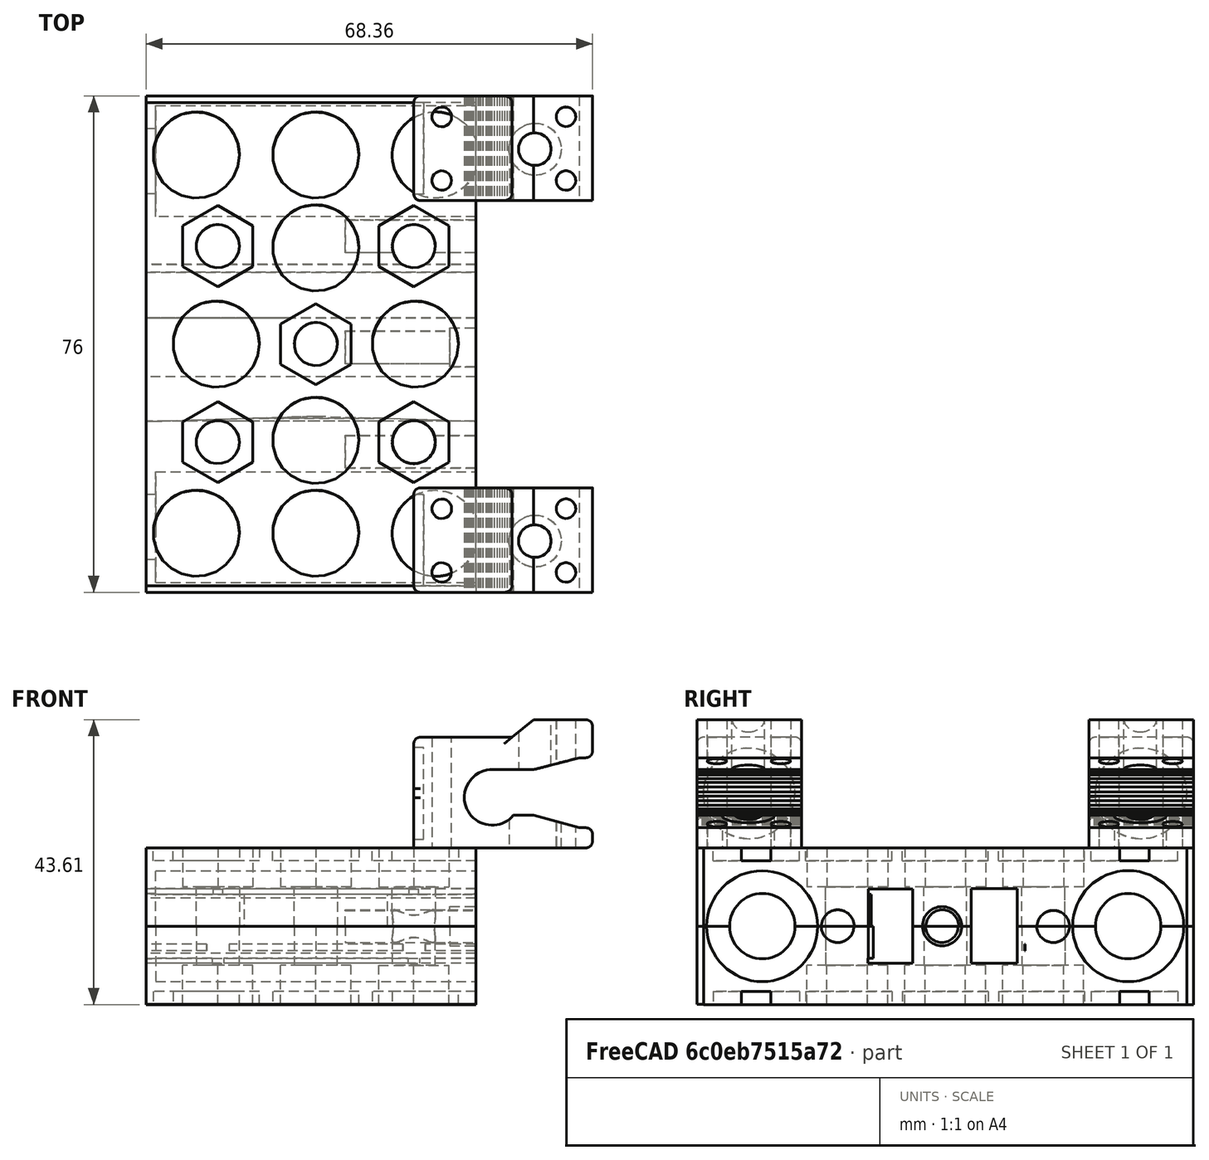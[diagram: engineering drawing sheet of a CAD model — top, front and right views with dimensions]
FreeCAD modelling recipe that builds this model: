
FCSTD DOCUMENT  (FreeCAD 0.21R33694 (Git))
Label: Universal_Axis_Z_Carriage
License: All rights reserved
LicenseURL: http://en.wikipedia.org/wiki/All_rights_reserved
objects: App::FeaturePython×12, Part::FeaturePython×3, Part::Compound×1
note: 4 computed .brp shape members not serialized (recipe doc carries the construction recipe); baked Part::Feature solids carry a one-line shape summary decoded from their .brp

FEATURE [Part::FeaturePython] b_Universal_Axis_Carriage_001_  label="Universal_Axis_Carriage_001"  # a2plus imported part (geometry in sourceFile) (typed FeaturePython)
  a2p_Version = 0.4.60n
  fixedPosition = true
  objectType = a2pPart
  sourceFile = ./Universal_Axis_Carriage.fcstd
  subassemblyImport = false
  timeLastImport = 1.70034e+09
  updateColors = true
FEATURE [Part::FeaturePython] b_Autoparallel_001_  label="Autoparallel_001"  # a2plus imported part (geometry in sourceFile) (typed FeaturePython)
  Placement = pos=(33.3346,-22,28.966) rot=(0,0.707107,-0.707107;3.14159rad)
  a2p_Version = 0.4.60n
  fixedPosition = false
  objectType = a2pPart
  sourceFile = ./Autoparallel.fcstd
  subassemblyImport = false
  timeLastImport = 1.68351e+09
  updateColors = true
FEATURE [App::FeaturePython] planeCoincident_001  label="planeCoincident_001__Universal_Axis_Carriage_001"  # a2plus constraint (typed FeaturePython)
  Object1 = b_Autoparallel_001_
  Object2 = b_Universal_Axis_Carriage_001_
  ParentTreeObject = -> b_Autoparallel_001_
  SubElement1 = Face15
  SubElement2 = Face156
  Suppressed = false
  Type = plane
  directionConstraint = 0
  offset = 0
FEATURE [App::FeaturePython] planeCoincident_001_mirror  label="planeCoincident_001__Autoparallel_001"  # a2plus constraint (typed FeaturePython)
  Object1 = b_Autoparallel_001_
  Object2 = b_Universal_Axis_Carriage_001_
  ParentTreeObject = -> b_Universal_Axis_Carriage_001_
  SubElement1 = Face15
  SubElement2 = Face156
  Suppressed = false
  Type = plane
  directionConstraint = 0
  offset = 0
FEATURE [App::FeaturePython] planeCoincident_002  label="planeCoincident_002__Universal_Axis_Carriage_001"  # a2plus constraint (typed FeaturePython)
  Object1 = b_Autoparallel_001_
  Object2 = b_Universal_Axis_Carriage_001_
  ParentTreeObject = -> b_Autoparallel_001_
  SubElement1 = Face74
  SubElement2 = Face128
  Suppressed = false
  Type = plane
  directionConstraint = 0
  offset = -8
FEATURE [App::FeaturePython] planeCoincident_002_mirror  label="planeCoincident_002__Autoparallel_001"  # a2plus constraint (typed FeaturePython)
  Object1 = b_Autoparallel_001_
  Object2 = b_Universal_Axis_Carriage_001_
  ParentTreeObject = -> b_Universal_Axis_Carriage_001_
  SubElement1 = Face74
  SubElement2 = Face128
  Suppressed = false
  Type = plane
  directionConstraint = 0
  offset = -8
FEATURE [App::FeaturePython] planeCoincident_003  label="planeCoincident_003__Autoparallel_001"  # a2plus constraint (typed FeaturePython)
  Object1 = b_Universal_Axis_Carriage_001_
  Object2 = b_Autoparallel_001_
  ParentTreeObject = -> b_Universal_Axis_Carriage_001_
  SubElement1 = Face230
  SubElement2 = Face52
  Suppressed = false
  Type = plane
  directionConstraint = 1
  offset = 0
FEATURE [App::FeaturePython] planeCoincident_003_mirror  label="planeCoincident_003__Universal_Axis_Carriage_001"  # a2plus constraint (typed FeaturePython)
  Object1 = b_Universal_Axis_Carriage_001_
  Object2 = b_Autoparallel_001_
  ParentTreeObject = -> b_Autoparallel_001_
  SubElement1 = Face230
  SubElement2 = Face52
  Suppressed = false
  Type = plane
  directionConstraint = 1
  offset = 0
FEATURE [Part::FeaturePython] b_Autoparallel_001_001  label="Autoparallel_002"  # a2plus imported part (geometry in sourceFile) (typed FeaturePython)
  Placement = pos=(33.3346,38,28.966) rot=(0,0.707107,-0.707107;3.14159rad)
  a2p_Version = 0.4.60n
  fixedPosition = false
  objectType = a2pPart
  sourceFile = ./Autoparallel.fcstd
  subassemblyImport = false
  timeLastImport = 1.68351e+09
  updateColors = true
FEATURE [App::FeaturePython] planeCoincident_004  label="planeCoincident_004__Universal_Axis_Carriage_001"  # a2plus constraint (typed FeaturePython)
  Object1 = b_Autoparallel_001_001
  Object2 = b_Universal_Axis_Carriage_001_
  ParentTreeObject = -> b_Autoparallel_001_001
  SubElement1 = Face15
  SubElement2 = Face156
  Suppressed = false
  Type = plane
  directionConstraint = 0
  offset = 0
FEATURE [App::FeaturePython] planeCoincident_004_mirror  label="planeCoincident_004__Autoparallel_002"  # a2plus constraint (typed FeaturePython)
  Object1 = b_Autoparallel_001_001
  Object2 = b_Universal_Axis_Carriage_001_
  ParentTreeObject = -> b_Universal_Axis_Carriage_001_
  SubElement1 = Face15
  SubElement2 = Face156
  Suppressed = false
  Type = plane
  directionConstraint = 0
  offset = 0
FEATURE [App::FeaturePython] planeCoincident_005  label="planeCoincident_005__Universal_Axis_Carriage_001"  # a2plus constraint (typed FeaturePython)
  Object1 = b_Autoparallel_001_001
  Object2 = b_Universal_Axis_Carriage_001_
  ParentTreeObject = -> b_Autoparallel_001_001
  SubElement1 = Face1
  SubElement2 = Face237
  Suppressed = false
  Type = plane
  directionConstraint = 0
  offset = 0
FEATURE [App::FeaturePython] planeCoincident_005_mirror  label="planeCoincident_005__Autoparallel_002"  # a2plus constraint (typed FeaturePython)
  Object1 = b_Autoparallel_001_001
  Object2 = b_Universal_Axis_Carriage_001_
  ParentTreeObject = -> b_Universal_Axis_Carriage_001_
  SubElement1 = Face1
  SubElement2 = Face237
  Suppressed = false
  Type = plane
  directionConstraint = 0
  offset = 0
FEATURE [App::FeaturePython] planeCoincident_006  label="planeCoincident_006__Universal_Axis_Carriage_001"  # a2plus constraint (typed FeaturePython)
  Object1 = b_Autoparallel_001_001
  Object2 = b_Universal_Axis_Carriage_001_
  ParentTreeObject = -> b_Autoparallel_001_001
  SubElement1 = Face74
  SubElement2 = Face128
  Suppressed = false
  Type = plane
  directionConstraint = 0
  offset = -8
FEATURE [App::FeaturePython] planeCoincident_006_mirror  label="planeCoincident_006__Autoparallel_002"  # a2plus constraint (typed FeaturePython)
  Object1 = b_Autoparallel_001_001
  Object2 = b_Universal_Axis_Carriage_001_
  ParentTreeObject = -> b_Universal_Axis_Carriage_001_
  SubElement1 = Face74
  SubElement2 = Face128
  Suppressed = false
  Type = plane
  directionConstraint = 0
  offset = -8
FEATURE [Part::Compound] Compound
  Links = -> [b_Universal_Axis_Carriage_001_,b_Autoparallel_001_,b_Autoparallel_001_001]
